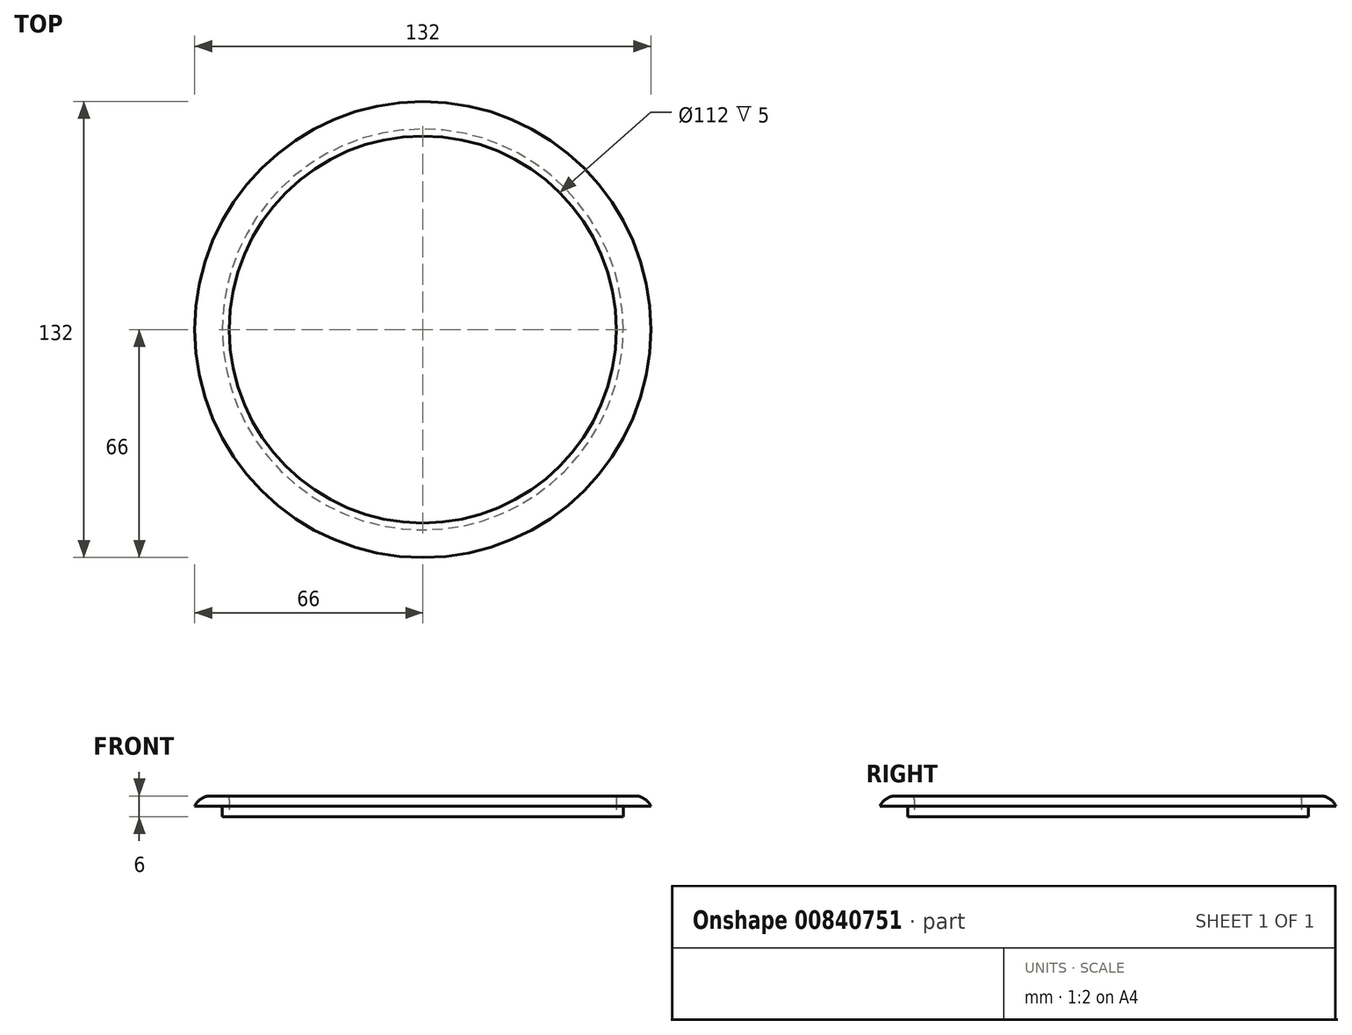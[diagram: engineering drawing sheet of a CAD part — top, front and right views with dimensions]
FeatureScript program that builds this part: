
annotation { "Feature Type Name" : "Feature", "Feature Type Description" : "" }
export const myFeature = defineFeature(function(context is Context, id is Id, definition is map)
    precondition{}
    {
        {
            var Q0;
            Q0=qCreatedBy(makeId("Top.planeOp"),FACE);
            var sketch = newSketch(context, id + "F0", { "sketchPlane" : qUnion([Q0])});
            skCircle(sketch, "E0", {"center": v(0, 0) * mm, "radius": 56 * mm});
            skCircle(sketch, "E1", {"center": v(0, 0) * mm, "radius": 58 * mm});
            skSolve(sketch);
        }
        {
            var Q0;
            Q0 = qSketchRegion(id + "F0", true);
            extrude(context, id + "F1", {"entities" : qUnion([Q0]), "depth" : 3 * mm, "offsetDistance" : 25 * mm});
        }
        {
            var Q0;
            Q0=makeQuery(id+"F1.opExtrude","CAP_FACE",FACE,{"disambiguationData":[OSD([sQuery(id+"F0.wireOp",EDGE,"E0"),sQuery(id+"F0.wireOp",EDGE,"E1")])],"isStart":false});
            var sketch = newSketch(context, id + "F2", { "sketchPlane" : qUnion([Q0])});
            skCircle(sketch, "E2", {"center": v(0, 0) * mm, "radius": 56 * mm});
            skCircle(sketch, "E3", {"center": v(0, 0) * mm, "radius": 66 * mm});
            skSolve(sketch);
        }
        {
            var Q0;
            Q0=makeQuery(id+"F2.imprint","IMPRINT",FACE,{"disambiguationData":[TD([[makeQuery(id+"F2.imprint","IMPRINT",EDGE,{"derivedFrom":sQuery(id+"F2.wireOp",EDGE,"E2")}),-1.0]])]});
            var Q1;
            Q1=makeQuery(id+"F2.imprint","IMPRINT",FACE,{"disambiguationData":[TD([[makeQuery(id+"F2.imprint","IMPRINT",EDGE,{"derivedFrom":sQuery(id+"F2.wireOp",EDGE,"E3")}),1.0]])]});
            extrude(context, id + "F3", {"entities" : qUnion([Q0, Q1]), "operationType" : NewBodyOperationType.ADD, "depth" : 3 * mm, "offsetDistance" : 25 * mm});
        }
        {
            var Q0;
            Q0=makeQuery(id+"F3.opExtrude","CAP_EDGE",EDGE,{"disambiguationData":[OSD([sQuery(id+"F2.wireOp",EDGE,"E3")])],"isStart":false});
            fillet(context, id + "F4", {"entities" : qUnion([Q0]), "radius" : 5 * mm, "tangentPropagation" : true, "allowEdgeOverflow" : false});
        }
        {
            var Q0;
            Q0=makeQuery(id+"F3.opExtrude","CAP_EDGE",EDGE,{"disambiguationData":[OSD([sQuery(id+"F2.wireOp",EDGE,"E2")])],"isStart":false});
            fillet(context, id + "F5", {"entities" : qUnion([Q0]), "radius" : 1 * mm, "tangentPropagation" : true, "allowEdgeOverflow" : false});
        }
    });
